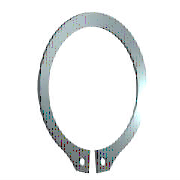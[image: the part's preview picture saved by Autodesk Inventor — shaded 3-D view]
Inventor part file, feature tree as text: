
AUTODESK INVENTOR PART (.ipt)
format: ipt  version: 2025 (Build 290162010, 162A)  size: 150,528 bytes
history: native  units: mm (DEFAULTED — no unit token found)
features: other x1, plane x1
ambient origin geometry x8: Origin, YZ Plane, XZ Plane, XY Plane, X Axis, Y Axis, Z Axis, Center Point
bodies: Solid1 (feature_tree), Body (feature_tree)
feature tree (2):
  other  "Work Axis1"
  plane  "Work Plane1"
